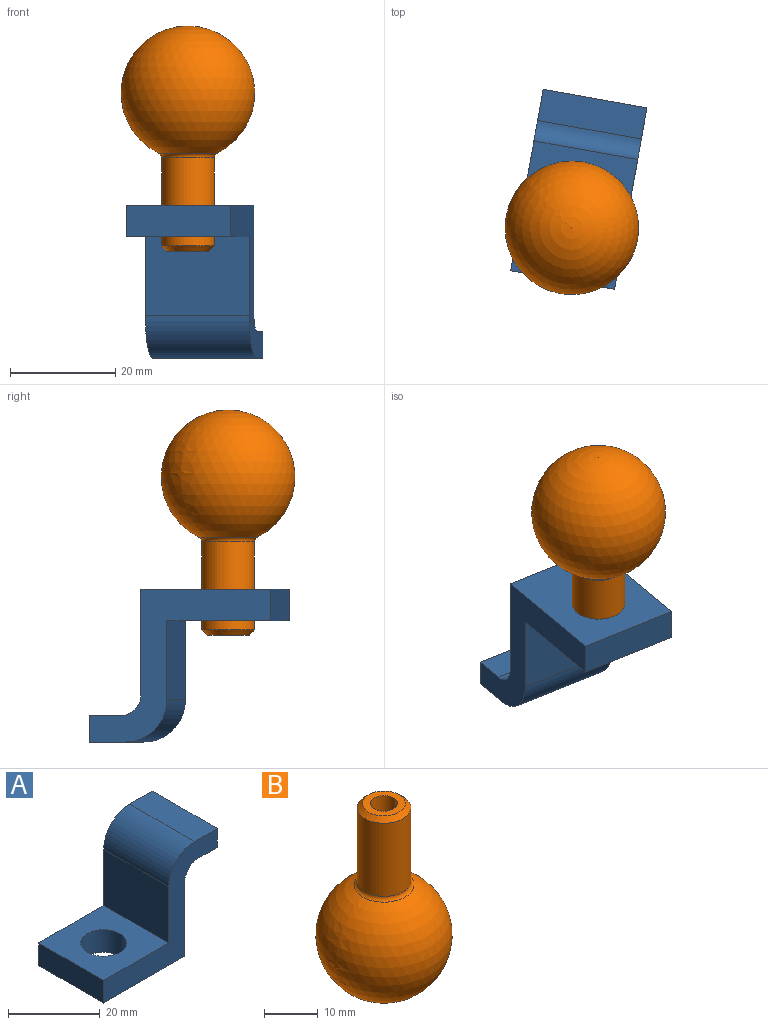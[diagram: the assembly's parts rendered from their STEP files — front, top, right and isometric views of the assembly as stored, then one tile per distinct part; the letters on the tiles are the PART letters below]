
ASSEMBLY  parts=2 mates=1
PART A: 13 faces, bbox 35x20x29 mm
  f0: plane 20x5mm, normal (1,0,0), area 100mm2, adj f1,f9,f10,f11
  f1: plane 20x7mm, normal (0,0,1), area 140mm2, adj f0,f2,f10,f11
  f2: cylinder r=8mm len=20mm, axis (0,1,0), area 251.3mm2, adj f1,f3,f10,f11
  f3: plane 20x15mm, normal (-1,0,0), area 300mm2, adj f2,f4,f10,f11
  f4: plane 20x20mm, normal (0,0,1), area 321.5mm2, adj f3,f5,f10,f11,f12
  f5: plane 20x6mm, normal (-1,0,0), area 120mm2, adj f4,f6,f10,f11
  f6: plane 25x20mm, normal (0,0,-1), area 421.5mm2, adj f5,f7,f10,f11,f12
  f7: plane 20x20mm, normal (1,0,0), area 400mm2, adj f6,f8,f10,f11
  f8: cylinder r=4mm len=20mm, axis (0,1,0), area 125.7mm2, adj f7,f9,f10,f11
  f9: plane 20x6mm, normal (0,0,-1), area 120mm2, adj f0,f8,f10,f11
  f10: plane 35x29mm, normal (0,-1,0), area 304.7mm2, adj f0,f1,f2,f3,f4,f5,f6,f7
  f11: plane 35x29mm, normal (0,1,0), area 304.7mm2, adj f0,f1,f2,f3,f4,f5,f6,f7
  f12: cylinder r=5mm len=10mm, axis (0,0,1), area 188.5mm2, adj f4,f6
PART B: 7 faces, bbox 25.4x25.4x42.7 mm
  f0: sphere r=12.7mm, area 19.8mm2, adj f1
  f1: cylinder r=2.5mm len=17.55mm, axis (0,0,-1), area 275.7mm2, adj f0,f2
  f2: plane 8x8mm, normal (0,0,1), area 30.6mm2, adj f1,f5
  f3: cylinder r=5mm len=16.68mm, axis (0,0,-1), area 524.1mm2, adj f5,f6
  f4: sphere r=12.7mm, area 1924.5mm2, adj f6
  f5: cone r=5mm half-angle=45deg, axis (0,0,-1), area 40mm2, adj f2,f3
  f6: torus R=6mm, axis (0,0,-1), area 36.5mm2, adj f3,f4
PLACE A rot(axis=(0.77,0.64,0),180deg) t=(0,0,-3)mm
PLACE B rot(axis=(0.92,-0.38,0),180deg) t=(0,0,24.29)mm
MATE cylindrical A.f12 <-> B.f1  axis (0,0,-1) through (0,0,3)mm
